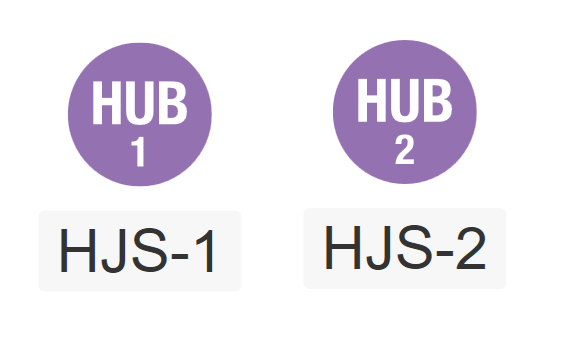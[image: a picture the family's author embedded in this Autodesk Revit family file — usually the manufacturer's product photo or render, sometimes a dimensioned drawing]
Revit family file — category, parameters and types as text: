
# Revit family: CSensor-Lutron-Ceiling-Vive_Series-HJS-1-SM
name_source: partatom
category: Lighting Devices
units: mm (PartAtom-declared; Revit-internal decimal feet)

## family parameters
Cut with Voids When Loaded = No
Host = Face
Maintain Annotation Orientation = Yes
OmniClass Number = 23.85.80.11.27
OmniClass Title = Lighting Controls
Part Type = Normal
Room Calculation Point = No
Round Connector Dimension = Use Diameter
Shared = No

## types (1)
- HJS-1-SM
    Apparent Load = 0 VA
    Assembly Code = D5030800
    Cost = 0 $
    Coverage = 15836.00 SF
    Coverage Area = 360˚ coverage from 71 ft (22 m)
    Coverage Range = 71 ft (22 m)
    Coverge Radius = 71' - 0"
    Default Elevation = 0' - 0"
    Depth = 0' - 4 39/128"
    Description = Vive hub, surface-mount adapter and power supply
    Finish = Plastic - Lutron - White Gloss
    Instruction Sheet Link = https://assets.lutron.com
    Keynote = Division 11
    Length = 0' - 6 103/128"
    Load Classification = Other
    Manufacturer = Lutron Electronics Co., Inc
    Manufacturer Fax Number = 610-282-1243
    Maximum Operating Temperature = 104 °F
    Minimum Operating Temperature = 32 °F
    Model = HJS-1-SM
    Performance URL = https://www.lutron.com
    Product Documentation Link = https://assets.lutron.com
    Product Name = Vive Wireless Hub
    Product Page URL = https://commercial.lutron.com
    Sensor Material = Plastic - Lutron - White Gloss
    Sensor Type = Occupancy/Vacancy
    Series = Vive Series
    URL = http://www.lutron.com
    Version = 2021 - v1.0a
    Video Link = https://www.youtube.com
    Voltage = 120 V
    Voltage Comments = Input to power supply: 120 – 277 V~ 50/60 Hz 0.6 A • Input to Vive hub: 24 V- 350 mA
    Warranty URL = https://www.lutron.com
    Width = 0' - 6 103/128"

## geometry (parser evidence)
native form markers: Sweep x5
no freeform markers — native parametric forms only
